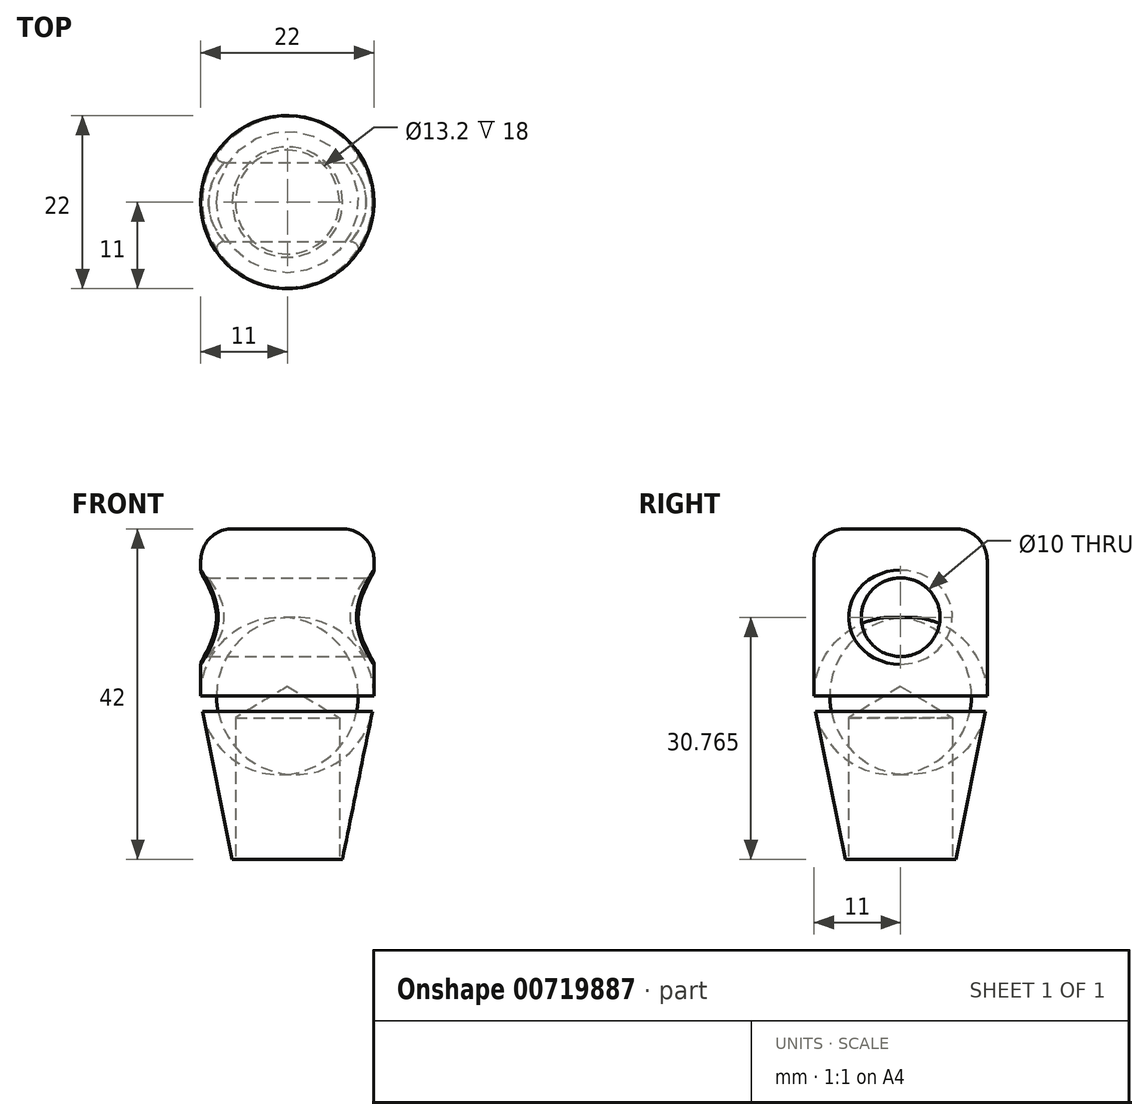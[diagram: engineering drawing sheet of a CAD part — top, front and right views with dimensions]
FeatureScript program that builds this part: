
annotation { "Feature Type Name" : "Feature", "Feature Type Description" : "" }
export const myFeature = defineFeature(function(context is Context, id is Id, definition is map)
    precondition{}
    {
        {
            var Q0;
            Q0=qCreatedBy(makeId("Front.planeOp"),FACE);
            var sketch = newSketch(context, id + "F0", { "sketchPlane" : qUnion([Q0])});
            skLineSegment(sketch, "E0", {"start": v(10.8, -3.17) * mm, "end": v(7, -21.95) * mm});
            skLineSegment(sketch, "E1", {"start": v(7, -21.95) * mm, "end": v(0, -21.95) * mm});
            skArc(sketch, "E2.filletArc", {"start": v(10.8, -3.17) * mm, "mid": v(10.95, -2.18) * mm, "end": v(11, -1.19) * mm});
            skPoint(sketch, "E3.visualSharp", {"position": v(11, 20.05) * mm});
            skLineSegment(sketch, "E4", {"start": v(0, 20.05) * mm, "end": v(0, -21.95) * mm});
            skLineSegment(sketch, "E5", {"start": v(0, 20.05) * mm, "end": v(7, 20.05) * mm});
            skLineSegment(sketch, "E6", {"start": v(11, -1.19) * mm, "end": v(11, 16.05) * mm});
            skLineSegment(sketch, "E7", {"start": v(11, 16.05) * mm, "end": v(11, 16.05) * mm});
            skArc(sketch, "E8.filletArc", {"start": v(11, 16.05) * mm, "mid": v(9.83, 18.88) * mm, "end": v(7, 20.05) * mm});
            skSolve(sketch);
        }
        {
            var Q0;
            Q0=makeQuery(id+"F0.imprint","IMPRINT",FACE,{"disambiguationData":[TD([[makeQuery(id+"F0.imprint","IMPRINT",EDGE,{"derivedFrom":sQuery(id+"F0.wireOp",EDGE,"E0")}),-1.0]])]});
            var Q1;
            Q1=sQuery(id+"F0.wireOp",EDGE,"E4");
            revolve(context, id + "F1", {"surfaceOperationType" : NewSurfaceOperationType.NEW, "entities" : qUnion([Q0]), "axis" : qUnion([Q1]), "revolveType" : RevolveType.FULL});
        }
        {
            var Q0;
            Q0=qCreatedBy(makeId("Right.planeOp"),FACE);
            var sketch = newSketch(context, id + "F2", { "sketchPlane" : qUnion([Q0])});
            skCircle(sketch, "E9", {"center": v(0, 8.81) * mm, "radius": 5 * mm});
            skSolve(sketch);
        }
        {
            var Q0;
            Q0 = qSketchRegion(id + "F2", true);
            extrude(context, id + "F3", {"entities" : qUnion([Q0]), "operationType" : NewBodyOperationType.REMOVE, "oppositeDirection" : true, "depth" : 25 * mm, "offsetDistance" : 25 * mm, "hasSecondDirection" : true, "secondDirectionOppositeDirection" : false, "secondDirectionDepth" : 25 * mm});
        }
        {
            var Q0;
            Q0=makeQuery(id+"F3.boolean.opBoolean","COPY",FACE,{"derivedFrom":makeQuery(id+"F3.opExtrude","SWEPT_FACE",FACE,{"disambiguationData":[OSD([sQuery(id+"F2.wireOp",EDGE,"E9")])]})});
            fillet(context, id + "F4", {"entities" : qUnion([Q0]), "radius" : 1 * mm, "tangentPropagation" : true, "allowEdgeOverflow" : false});
        }
        {
            var Q0;
            Q0=makeQuery(id+"F1.opRevolve","SWEPT_FACE",FACE,{"disambiguationData":[OSD([sQuery(id+"F0.wireOp",EDGE,"E1")])]});
            var sketch = newSketch(context, id + "F5", { "sketchPlane" : qUnion([Q0])});
            skPoint(sketch, "E10", {"position": v(0, 0) * mm});
            skSolve(sketch);
        }
        {
            var Q0;
            Q0=sQuery(id+"F5.wireOp",VERTEX,"E10");
            var Q1;
            Q1=makeQuery(id+"F1.opRevolve","SWEPT_BODY",BODY,{"disambiguationData":[OSD([sQuery(id+"F0.wireOp",EDGE,"CHDU2zw6-gQqM-ajkK-WM8U-mchMsUYrqzLO"),sQuery(id+"F0.wireOp",EDGE,"SZNWTcXt-H34u-H7aS-kSzI-nm8D3oyar36U"),sQuery(id+"F0.wireOp",EDGE,"E0"),sQuery(id+"F0.wireOp",EDGE,"E1"),sQuery(id+"F0.wireOp",EDGE,"E2.filletArc"),sQuery(id+"F0.wireOp",EDGE,"E3.filletArc"),sQuery(id+"F0.wireOp",EDGE,"E4")])]});
            hole(context, id + "F6", {"style" : HoleStyle.SIMPLE, "endStyle" : HoleEndStyle.BLIND, "standardTappedOrClearance" : lookupTablePath({ "standard" : "ISO", "fit" : "Normal", "size" : "M12", "type" : "Clearance" }), "standardBlindInLast" : lookupTablePath({ "fit" : "Standard", "standard" : "ISO", "size" : "M12", "type" : "Clearance" }), "holeDiameter" : 13.2 * mm, "majorDiameter" : 12 * mm, "holeDepth" : 18 * mm, "isTappedThrough" : true, "tappedDepth" : 12 * mm, "tapClearance" : 3, "locations" : qUnion([Q0]), "scope" : qUnion([Q1])});
        }
    });
